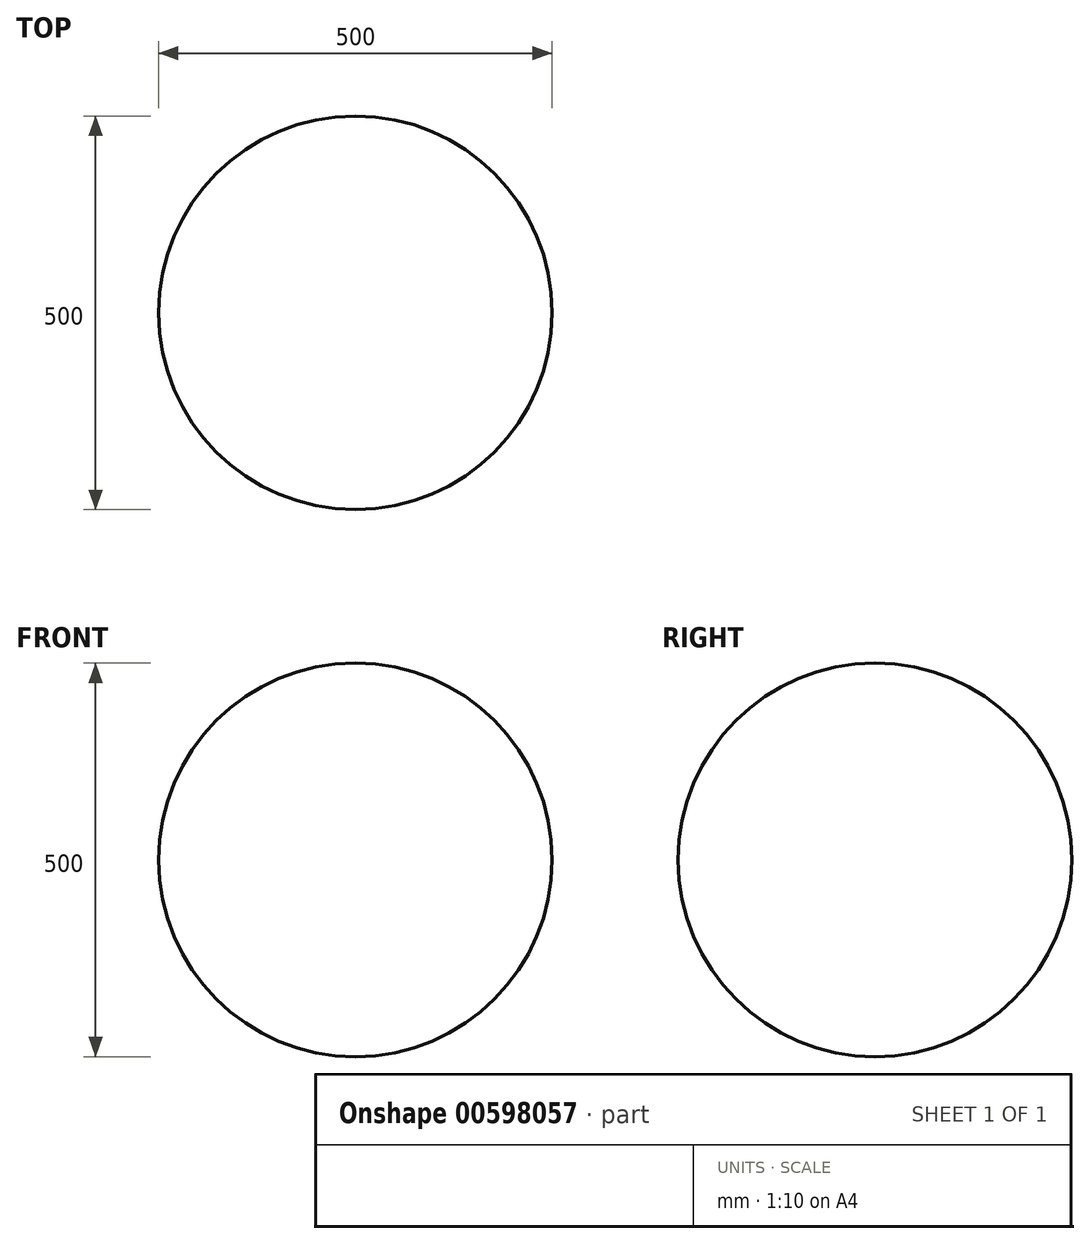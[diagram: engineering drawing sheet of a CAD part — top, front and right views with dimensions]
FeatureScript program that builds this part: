
annotation { "Feature Type Name" : "Feature", "Feature Type Description" : "" }
export const myFeature = defineFeature(function(context is Context, id is Id, definition is map)
    precondition{}
    {
        {
            var Q0;
            Q0=qCreatedBy(makeId("Top.planeOp"),FACE);
            var sketch = newSketch(context, id + "F0", { "sketchPlane" : qUnion([Q0])});
            skLineSegment(sketch, "E0", {"start": v(0, 250) * mm, "end": v(0, -250) * mm});
            skArc(sketch, "E1", {"start": v(0, -250) * mm, "mid": v(250, 0) * mm, "end": v(0, 250) * mm});
            skSolve(sketch);
        }
        {
            var Q0;
            Q0 = qSketchRegion(id + "F0", true);
            var Q1;
            Q1=sQuery(id+"F0.wireOp",EDGE,"E0");
            revolve(context, id + "F1", {"entities" : qUnion([Q0]), "axis" : qUnion([Q1]), "revolveType" : RevolveType.FULL});
        }
    });
